# Revit family: Building-IEC309Connections-GEWISS-67IB-INTERLOCKED-SOCKET-OUTLETS_IP67_WITHOUT_BOTTOM
name_source: partatom
category: Apparecchi elettrici
units: mm (PartAtom-declared; Revit-internal decimal feet)

## family parameters
Condiviso = Sì
Host = Superficie
Mantenere orientamento annotazione = Sì
Punto di calcolo locali = Sì
Quota connettore circolare = Usa diametro
Taglio con vuoti quando caricato = Sì
Tipo di parte = Normale

## types (23) — shared parameters
Catalogue = BUILDING
Catalogue Range = 67 IB
Corpo presa = GEWISS -BLU
Electrocod = 2222
Frequency = 50/60 Hz
Glow Wire Test = 850 °C
Glow wire test: = 850 °C
IDF = d4539c21-b4dc-4599-b1fe-3d571a3ca594
IDT = c02ff193-3075-4b5a-ac4b-08e79c84e21a
IP degree = IP67
Immagine tipo = C.jpg
Operating temperature: = -25 +40 °C
Produttore = GEWISS S.p.A.
Prospetto di default = 1219 mm
Protection = NO (SBF)
Rated frequency (Hz) = 50/60 Hz
SEO = Socket outlet
Shock resistance = IK08
Simbolo presa = PRESAINDSTAGNA : 3P
Struttura = Grigio RAL - 7035
Technical sheet = https://www.gewiss.com
Thermo-pressure with ball = 125
Typology = Vertical
URL = https://www.gewiss.com
Version file RFA = 21.4
With back-mounting box = No
Working temperature = -25 ÷ +40 °C
presa = rosso
zero-valued in all types: giallo

## per-type parameters (varying)
| type | Colour | Colour: | Descrizione | EAN code | Modello | No. of poles | Number of poles | Rated current (A) | Rated current (In) | Rated voltage | Rated voltage: | Reference h |
| GW66315N - 32A 2P+E 230V V.INT.SOCK.O.N.B.6H SBF | Blue | Blue | 32A 2P+E 230V V.INT.SOCK.O.N.B.6H SBF | 8011564741706 | GW66315N | 2P+E | 2P+E | 32 | 32 | 200 - 250 V | 200 - 250 V | 6 |
| GW66317N - 32A 3P+N+E 230V V.INT.SOCK.O.N.B.9H SBF | Blue | Blue | 32A 3P+N+E 230V V.INT.SOCK.O.N.B.9H SBF | 8011564741720 | GW66317N | 3P+N+E | 3P+N+E | 32 | 32 | 200 - 250 V | 200 - 250 V | 9 |
| GW66309N - 16A 3P+N+E 400V V.INT.SOCK.O.N.B.9H SBF | Red | Red | 16A 3P+N+E 400V V.INT.SOCK.O.N.B.9H SBF | 8011564741645 | GW66309N | 3P+N+E | 3P+N+E | 16 | 16 | 380 - 415 V | 380 - 415 V | 6 |
| GW66304N - 16A 2P+E 230V V.INT.SOCK.O.N.B.6H SBF | Blue | Blue | 16A 2P+E 230V V.INT.SOCK.O.N.B.6H SBF | 8011564741591 | GW66304N | 2P+E | 2P+E | 16 | 16 | 200 - 250 V | 200 - 250 V | 6 |
| GW66307N - 16A 2P+E 400V V.INT.SOCK.O.N.B.6H SBF | Red | Red | 16A 2P+E 400V V.INT.SOCK.O.N.B.6H SBF | 8011564741621 | GW66307N | 2P+E | 2P+E | 16 | 16 | 380 - 415 V | 380 - 415 V | 9 |
| GW66316N - 32A 3P+E 230V V.INT.SOCK.O.N.B.9H SBF | Blue | Blue | 32A 3P+E 230V V.INT.SOCK.O.N.B.9H SBF | 8011564741713 | GW66316N | 3P+E | 3P+E | 32 | 32 | 200 - 250 V | 200 - 250 V | 9 |
| GW66312N - 32A 2P+E 110V V.INT.SOCK.O.N.B.4H SBF | Yellow | Yellow | 32A 2P+E 110V V.INT.SOCK.O.N.B.4H SBF | 8011564741676 | GW66312N | 2P+E | 2P+E | 32 | 32 | 100 - 130 V | 100 - 130 V | 4 |
| GW66318N - 32A 2P+E 400V V.INT.SOCK.O.N.B.6H SBF | Red | Red | 32A 2P+E 400V V.INT.SOCK.O.N.B.6H SBF | 8011564741737 | GW66318N | 2P+E | 2P+E | 32 | 32 | 380 - 415 V | 380 - 415 V | 9 |
| GW66301N - 16A 2P+E 110V V.INT.SOCK.O.N.B.4H SBF | Yellow | Yellow | 16A 2P+E 110V V.INT.SOCK.O.N.B.4H SBF | 8011564741560 | GW66301N | 2P+E | 2P+E | 16 | 16 | 100 - 130 V | 100 - 130 V | 4 |
| GW66313N - 32A 3P+E 110V V.INT.SOCK.O.N.B.4H SBF | Yellow | Yellow | 32A 3P+E 110V V.INT.SOCK.O.N.B.4H SBF | 8011564741683 | GW66313N | 3P+E | 3P+E | 32 | 32 | 100 - 130 V | 100 - 130 V | 4 |
| GW66310N - 16A 3P+E 500V V.INT.SOCK.O.N.B.7H SBF | Black | Black | 16A 3P+E 500V V.INT.SOCK.O.N.B.7H SBF | 8011564741652 | GW66310N | 3P+E | 3P+E | 16 | 16 | 480 - 500 V | 480 - 500 V | 7 |
| GW66320N - 32A 3P+N+E 400V V.INT.SOCK.O.N.B.9H SBF | Red | Red | 32A 3P+N+E 400V V.INT.SOCK.O.N.B.9H SBF | 8011564741751 | GW66320N | 3P+N+E | 3P+N+E | 32 | 32 | 380 - 415 V | 380 - 415 V | 6 |
| GW66306N - 16A 3P+N+E 230V V.INT.SOCK.O.N.B.9H SBF | Blue | Blue | 16A 3P+N+E 230V V.INT.SOCK.O.N.B.9H SBF | 8011564741614 | GW66306N | 3P+N+E | 3P+N+E | 16 | 16 | 200 - 250 V | 200 - 250 V | 9 |
| GW66305N - 16A 3P+E 230V V.INT.SOCK.O.N.B.9H SBF | Blue | Blue | 16A 3P+E 230V V.INT.SOCK.O.N.B.9H SBF | 8011564741607 | GW66305N | 3P+E | 3P+E | 16 | 16 | 200 - 250 V | 200 - 250 V | 9 |
| GW66314N - 32A 3P+N+E 110V V.INT.SOCK.O.N.B.4H SBF | Yellow | Yellow | 32A 3P+N+E 110V V.INT.SOCK.O.N.B.4H SBF | 8011564741690 | GW66314N | 3P+N+E | 3P+N+E | 32 | 32 | 100 - 130 V | 100 - 130 V | 4 |
| GW66302N - 16A 3P+E 110V V.INT.SOCK.O.N.B.4H SBF | Yellow | Yellow | 16A 3P+E 110V V.INT.SOCK.O.N.B.4H SBF | 8011564741577 | GW66302N | 3P+E | 3P+E | 16 | 16 | 100 - 130 V | 100 - 130 V | 4 |
| GW66319N - 32A 3P+E 400V V.INT.SOCK.O.N.B.9H SBF | Red | Red | 32A 3P+E 400V V.INT.SOCK.O.N.B.9H SBF | 8011564741744 | GW66319N | 3P+E | 3P+E | 32 | 32 | 380 - 415 V | 380 - 415 V | 6 |
| GW66357N - 32A 3P+E 380V V.INT.SOCK.O.N.B.3H SBF | Red | Red | 32A 3P+E 380V V.INT.SOCK.O.N.B.3H SBF | 8011564742116 | GW66357N | 3P+E | 3P+E | 32 | 32 | 380 - 440 V | 380 - 440 V | 3 |
| GW66322N - 32A 3P+N+E 500V V.INT.SOCK.O.N.B.7H SBF | Black | Black | 32A 3P+N+E 500V V.INT.SOCK.O.N.B.7H SBF | 8011564741775 | GW66322N | 3P+N+E | 3P+N+E | 32 | 32 | 480 - 500 V | 480 - 500 V | 7 |
| GW66308N - 16A 3P+E 400V V.INT.SOCK.O.N.B.9H SBF | Red | Red | 16A 3P+E 400V V.INT.SOCK.O.N.B.9H SBF | 8011564741638 | GW66308N | 3P+E | 3P+E | 16 | 16 | 380 - 415 V | 380 - 415 V | 6 |
| GW66303N - 16A 3P+N+E 110V V.INT.SOCK.O.N.B.4H SBF | Yellow | Yellow | 16A 3P+N+E 110V V.INT.SOCK.O.N.B.4H SBF | 8011564741584 | GW66303N | 3P+N+E | 3P+N+E | 16 | 16 | 100 - 130 V | 100 - 130 V | 4 |
| GW66311N - 16A 3P+N+E 500V V.INT.SOCK.O.N.B.7H SBF | Black | Black | 16A 3P+N+E 500V V.INT.SOCK.O.N.B.7H SBF | 8011564741669 | GW66311N | 3P+N+E | 3P+N+E | 16 | 16 | 480 - 500 V | 480 - 500 V | 7 |
| GW66321N - 32A 3P+E 500V V.INT.SOCK.O.N.B.7H SBF | Black | Black | 32A 3P+E 500V V.INT.SOCK.O.N.B.7H SBF | 8011564741768 | GW66321N | 3P+E | 3P+E | 32 | 32 | 480 - 500 V | 480 - 500 V | 7 |

note: source unit labels omitted for Thermo-pressure with ball — the stored unit's dimension contradicts the parameter name (converter mislabeling)

## geometry (parser evidence)
native form markers: Sweep x4
no freeform markers — native parametric forms only
